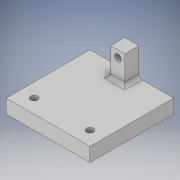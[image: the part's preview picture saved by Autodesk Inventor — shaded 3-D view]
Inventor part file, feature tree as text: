
AUTODESK INVENTOR PART (.ipt)
format: ipt  version: 2018 (Build 220112000, 112)  size: 123,904 bytes
history: native  units: in
note: dims shown in document units (in); Inventor stores cm internally (conversion verified against a paired STEP export)
features: sketch x5, hole x3, extrude x2, fillet x1
ambient origin geometry x8: Origin, YZ Plane, XZ Plane, XY Plane, X Axis, Y Axis, Z Axis, Center Point
bodies: Solid1 (feature_tree)
feature tree (11):
  extrude  "Extrusion1"  Depth=3.0in
  hole  "Hole1"  [1 undecoded]
  extrude  "Extrusion2"  Depth=1.0in TaperAngle=0.0deg
  hole  "Hole2"  [1 undecoded]
  fillet  "Fillet1"  [1 undecoded]
  hole  "Hole3"  [1 undecoded]
  sketch  "Sketch1"  dims[d0=3.0in d1=3.0in]
  sketch  "Sketch2"  dims[d2=0.5in d3=0.0in]
  sketch  "Sketch3"  dims[d4=0.2in d5=0.75in d6=0.375in d7=0.25in d8=0.5635in d9=0.375in d10=0.8108in d11=0.5in]
  sketch  "Sketch4"  dims[d12=0.5in d13=1.0in d14=0.0in]
  sketch  "Sketch5"  dims[d15=0.25in d16=0.75in d17=0.375in d18=0.25in d19=0.5635in d20=0.5625in d21=0.8108in d22=0.125in d23=0.25in d24=0.75in d25=0.375in d26=0.25in d27=0.5635in d28=0.375in d29=0.8108in]
note: 4 required parameter values undecoded (feature->parameter linkage not recoverable at this tier; creation-order binding heuristic only, values carry confidence <= 0.55)
